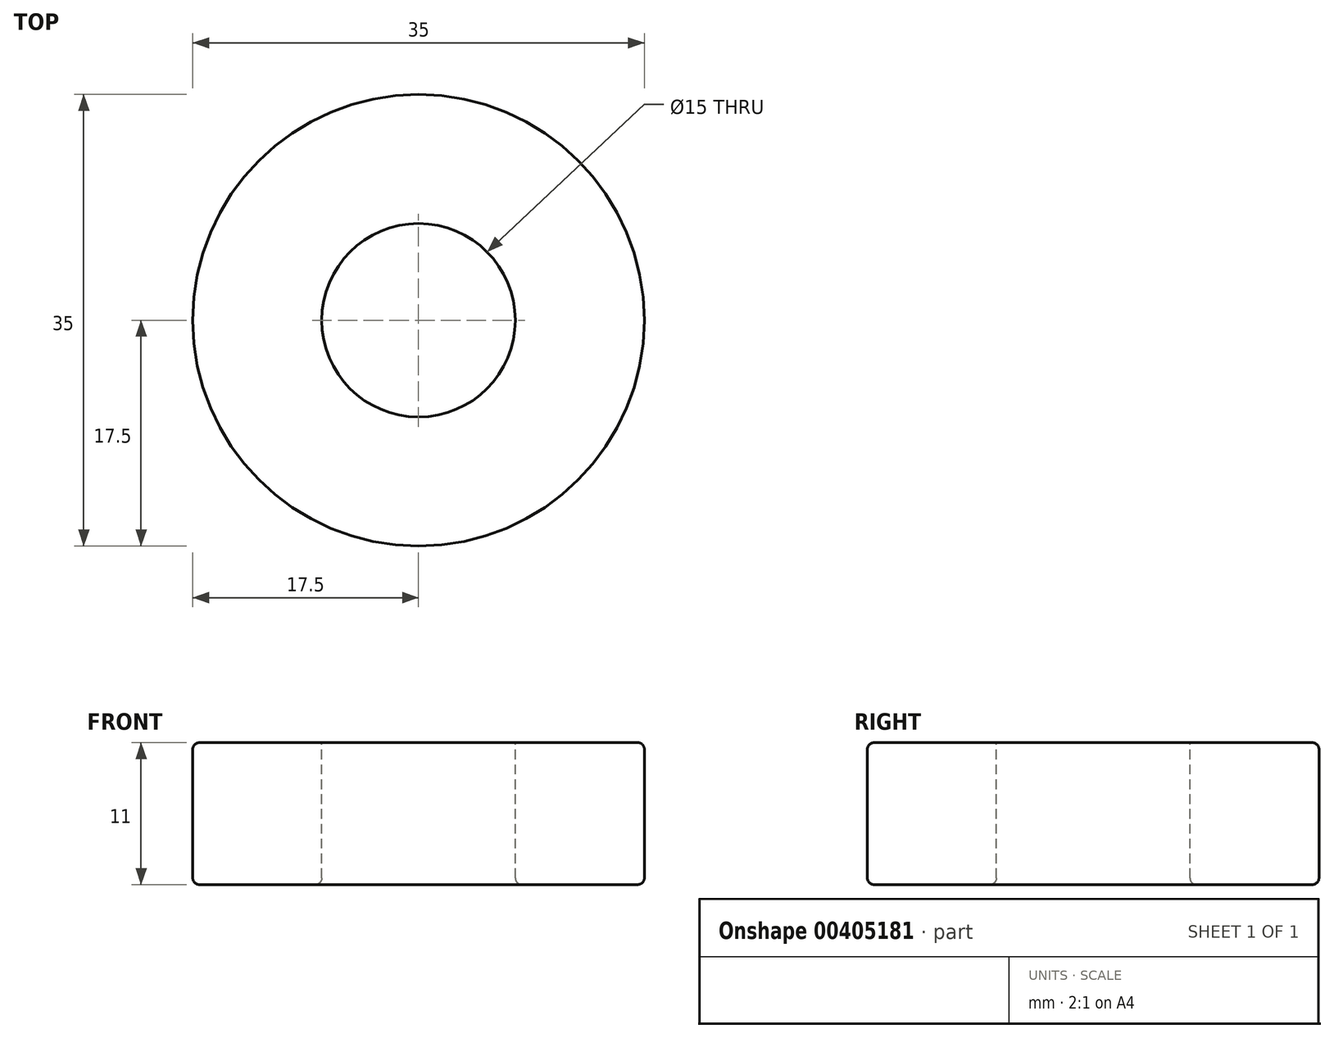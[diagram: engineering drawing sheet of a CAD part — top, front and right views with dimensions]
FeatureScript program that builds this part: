
annotation { "Feature Type Name" : "Feature", "Feature Type Description" : "" }
export const myFeature = defineFeature(function(context is Context, id is Id, definition is map)
    precondition{}
    {
        {
            var Q0;
            Q0=qCreatedBy(makeId("Top.planeOp"),FACE);
            var sketch = newSketch(context, id + "F0", { "sketchPlane" : qUnion([Q0])});
            skCircle(sketch, "E0", {"center": v(0, 0) * mm, "radius": 17.5 * mm});
            skSolve(sketch);
        }
        {
            var Q0;
            Q0 = qSketchRegion(id + "F0", true);
            extrude(context, id + "F1", {"entities" : qUnion([Q0]), "depth" : 11 * mm});
        }
        {
            var Q0;
            Q0=makeQuery(id+"F1.opExtrude","CAP_FACE",FACE,{"disambiguationData":[OSD([sQuery(id+"F0.wireOp",EDGE,"E0")])],"isStart":false});
            var sketch = newSketch(context, id + "F2", { "sketchPlane" : qUnion([Q0])});
            skCircle(sketch, "E1", {"center": v(0, 0) * mm, "radius": 7.5 * mm});
            skSolve(sketch);
        }
        {
            var Q0;
            Q0 = qSketchRegion(id + "F2", true);
            extrude(context, id + "F3", {"entities" : qUnion([Q0]), "operationType" : NewBodyOperationType.REMOVE, "endBound" : BoundingType.THROUGH_ALL, "oppositeDirection" : true, "depth" : 25 * mm});
        }
        {
            var Q0;
            Q0=makeQuery(id+"F1.opExtrude","CAP_EDGE",EDGE,{"disambiguationData":[OSD([sQuery(id+"F0.wireOp",EDGE,"E0")])],"isStart":false});
            var Q1;
            Q1=makeQuery(id+"F1.opExtrude","CAP_EDGE",EDGE,{"disambiguationData":[OSD([sQuery(id+"F0.wireOp",EDGE,"E0")])],"isStart":true});
            fillet(context, id + "F4", {"entities" : qUnion([Q0, Q1]), "radius" : 0.5 * mm, "tangentPropagation" : true, "allowEdgeOverflow" : false});
        }
        {
            var Q0;
            Q0=makeQuery(id+"F3.boolean.opBoolean","COPY",EDGE,{"derivedFrom":makeQuery(id+"F3.opExtrude","CAP_EDGE",EDGE,{"disambiguationData":[OSD([sQuery(id+"F2.wireOp",EDGE,"E1")])],"isStart":true})});
            var Q1;
            Q1=makeQuery(id+"F3.boolean.opBoolean","INTERSECT",EDGE,{"derivedFrom":[makeQuery(id+"F1.opExtrude","CAP_FACE",FACE,{"disambiguationData":[OSD([sQuery(id+"F0.wireOp",EDGE,"E0")])],"isStart":true}),makeQuery(id+"F3.opExtrude","SWEPT_FACE",FACE,{"disambiguationData":[OSD([sQuery(id+"F2.wireOp",EDGE,"E1")])]})]});
            fillet(context, id + "F5", {"entities" : qUnion([Q0, Q1]), "radius" : 0.5 * mm, "tangentPropagation" : true, "allowEdgeOverflow" : false});
        }
    });
